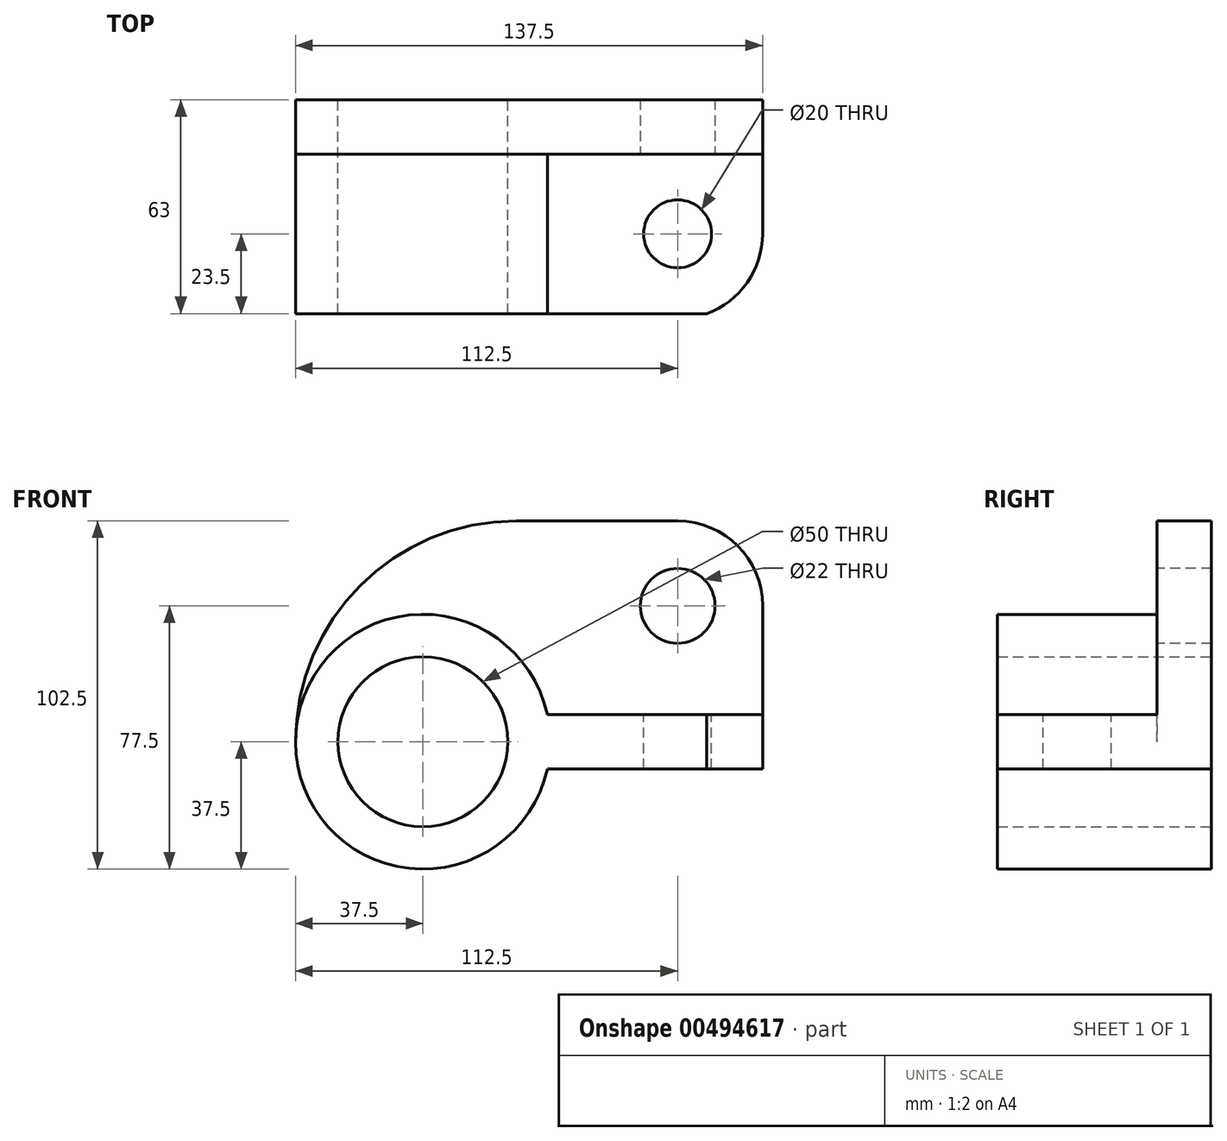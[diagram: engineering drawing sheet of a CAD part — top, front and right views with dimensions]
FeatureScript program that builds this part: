
annotation { "Feature Type Name" : "Feature", "Feature Type Description" : "" }
export const myFeature = defineFeature(function(context is Context, id is Id, definition is map)
    precondition{}
    {
        {
            var Q0;
            Q0=qCreatedBy(makeId("Front.planeOp"),FACE);
            var sketch = newSketch(context, id + "F0", { "sketchPlane" : qUnion([Q0])});
            skCircle(sketch, "E0", {"center": v(0, 0) * mm, "radius": 25 * mm});
            skArc(sketch, "E1", {"start": v(36.64, 8) * mm, "mid": v(-37.5, 0) * mm, "end": v(36.64, -8) * mm});
            skPoint(sketch, "E2.endSnap0", {"position": v(100, 4) * mm});
            skLineSegment(sketch, "E3", {"start": v(100, 8) * mm, "end": v(36.64, 8) * mm});
            skLineSegment(sketch, "E4", {"start": v(36.64, -8) * mm, "end": v(100, -8) * mm});
            skPoint(sketch, "E5.trimOffspring.start.orphan", {"position": v(100, 0) * mm});
            skLineSegment(sketch, "E6", {"start": v(100, 8) * mm, "end": v(100, -8) * mm});
            skSolve(sketch);
        }
        {
            var Q0;
            Q0=makeQuery(id+"F0.imprint","IMPRINT",FACE,{"disambiguationData":[TD([[makeQuery(id+"F0.imprint","IMPRINT",EDGE,{"derivedFrom":sQuery(id+"F0.wireOp",EDGE,"E0")}),-1.0]])]});
            extrude(context, id + "F1", {"entities" : qUnion([Q0]), "endBound" : BoundingType.SYMMETRIC, "depth" : 47 * mm});
        }
        {
            var Q0;
            Q0=makeQuery(id+"F1.opExtrude","SWEPT_FACE",FACE,{"disambiguationData":[OSD([sQuery(id+"F0.wireOp",EDGE,"E3")])]});
            var sketch = newSketch(context, id + "F2", { "sketchPlane" : qUnion([Q0])});
            skPoint(sketch, "E7.end.orphan", {"position": v(100, 0) * mm});
            skPoint(sketch, "E8.start.orphan", {"position": v(68.32, -23.5) * mm});
            skCircle(sketch, "E9", {"center": v(75, 0) * mm, "radius": 10 * mm});
            skArc(sketch, "E10", {"start": v(83.53, -23.5) * mm, "mid": v(95.47, -14.35) * mm, "end": v(100, 0) * mm});
            skLineSegment(sketch, "E11", {"start": v(100, 0) * mm, "end": v(100, -23.5) * mm});
            skLineSegment(sketch, "E12", {"start": v(100, -23.5) * mm, "end": v(83.53, -23.5) * mm});
            skSolve(sketch);
        }
        {
            var Q0;
            Q0=makeQuery(id+"F2.imprint","IMPRINT",FACE,{"disambiguationData":[TD([[makeQuery(id+"F2.imprint","IMPRINT",EDGE,{"derivedFrom":sQuery(id+"F2.wireOp",EDGE,"E9")}),1.0]])]});
            var Q1;
            Q1=makeQuery(id+"F2.imprint","IMPRINT",FACE,{"disambiguationData":[TD([[makeQuery(id+"F2.imprint","IMPRINT",EDGE,{"derivedFrom":sQuery(id+"F2.wireOp",EDGE,"E11")}),1.0]])]});
            extrude(context, id + "F3", {"entities" : qUnion([Q0, Q1]), "operationType" : NewBodyOperationType.REMOVE, "oppositeDirection" : true, "depth" : 25 * mm});
        }
        {
            var Q0;
            Q0=makeQuery(id+"F1.opExtrude","CAP_FACE",FACE,{"disambiguationData":[OSD([sQuery(id+"F0.wireOp",EDGE,"E0"),sQuery(id+"F0.wireOp",EDGE,"E1"),sQuery(id+"F0.wireOp",EDGE,"E3"),sQuery(id+"F0.wireOp",EDGE,"E4"),sQuery(id+"F0.wireOp",EDGE,"E6")])],"isStart":true});
            var sketch = newSketch(context, id + "F4", { "sketchPlane" : qUnion([Q0])});
            skLineSegment(sketch, "E13", {"start": v(-23.69, -8) * mm, "end": v(-100, -8) * mm});
            skLineSegment(sketch, "E14", {"start": v(-100, -8) * mm, "end": v(-100, 8) * mm});
            skLineSegment(sketch, "E15", {"start": v(-100, 8) * mm, "end": v(-100, 40) * mm});
            skCircle(sketch, "E16", {"center": v(-75, 40) * mm, "radius": 11 * mm});
            skArc(sketch, "E17", {"start": v(-75, 65) * mm, "mid": v(-92.68, 57.68) * mm, "end": v(-100, 40) * mm});
            skLineSegment(sketch, "E18", {"start": v(-75, 65) * mm, "end": v(0, 65) * mm});
            skArc(sketch, "E19", {"start": v(0, 25) * mm, "mid": v(-20.31, 14.58) * mm, "end": v(-23.69, -8) * mm});
            skArc(sketch, "E20", {"start": v(37.5, 0) * mm, "mid": v(29.08, 38.46) * mm, "end": v(0, 65) * mm});
            skSolve(sketch);
        }
        {
            var Q0;
            Q0=makeQuery(id+"F4.imprint","IMPRINT",FACE,{"disambiguationData":[TD([[makeQuery(id+"F4.imprint","IMPRINT",EDGE,{"derivedFrom":sQuery(id+"F4.wireOp",EDGE,"E15")}),-1.0]])]});
            extrude(context, id + "F5", {"entities" : qUnion([Q0]), "operationType" : NewBodyOperationType.ADD, "depth" : (63 - 47) * mm});
        }
        {
            var Q0;
            Q0=makeQuery(id+"F1.opExtrude","CAP_FACE",FACE,{"disambiguationData":[OSD([sQuery(id+"F0.wireOp",EDGE,"E0"),sQuery(id+"F0.wireOp",EDGE,"E1"),sQuery(id+"F0.wireOp",EDGE,"E3"),sQuery(id+"F0.wireOp",EDGE,"E4"),sQuery(id+"F0.wireOp",EDGE,"E6")])],"isStart":true});
            extrude(context, id + "F6", {"entities" : qUnion([Q0]), "operationType" : NewBodyOperationType.ADD, "depth" : (63 - 47) * mm});
        }
        {
            var Q0;
            Q0=makeQuery(id+"F5.opExtrude","SWEPT_EDGE",EDGE,{"disambiguationData":[OSD([sQuery(id+"F4.wireOp",EDGE,"E18"),sQuery(id+"F4.wireOp",EDGE,"E20")])]});
            fillet(context, id + "F7", {"entities" : qUnion([Q0]), "radius" : 65 * mm, "tangentPropagation" : true, "allowEdgeOverflow" : false});
        }
    });
